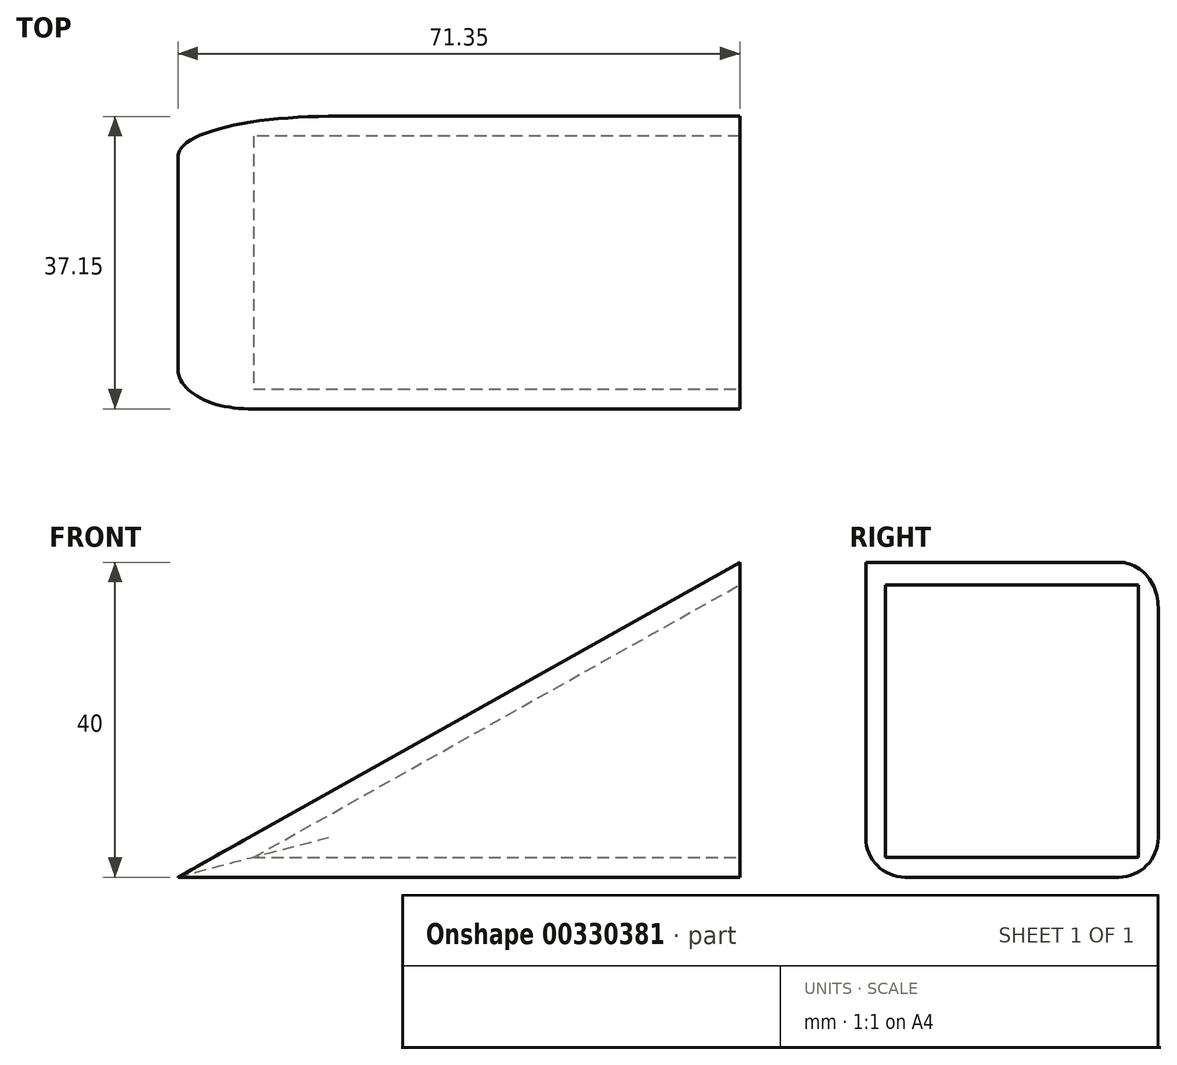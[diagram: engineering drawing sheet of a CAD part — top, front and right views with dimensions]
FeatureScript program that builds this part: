
annotation { "Feature Type Name" : "Feature", "Feature Type Description" : "" }
export const myFeature = defineFeature(function(context is Context, id is Id, definition is map)
    precondition{}
    {
        {
            var Q0;
            Q0=qCreatedBy(makeId("Top.planeOp"),FACE);
            var sketch = newSketch(context, id + "F0", { "sketchPlane" : qUnion([Q0])});
            skLineSegment(sketch, "E0.bottom", {"start": v(-52.14, 32.68) * mm, "end": v(19.21, 32.68) * mm});
            skLineSegment(sketch, "E0.top", {"start": v(-52.14, -4.47) * mm, "end": v(19.21, -4.47) * mm});
            skLineSegment(sketch, "E0.left", {"start": v(-52.14, 32.68) * mm, "end": v(-52.14, -4.47) * mm});
            skLineSegment(sketch, "E0.right", {"start": v(19.21, 32.68) * mm, "end": v(19.21, -4.47) * mm});
            skSolve(sketch);
        }
        {
            var Q0;
            Q0=makeQuery(id+"F0.imprint","IMPRINT",FACE,{"disambiguationData":[TD([[makeQuery(id+"F0.imprint","IMPRINT",EDGE,{"derivedFrom":sQuery(id+"F0.wireOp",EDGE,"E0.bottom")}),-1.0]])]});
            extrude(context, id + "F1", {"entities" : qUnion([Q0]), "depth" : 40 * mm});
        }
        {
            var Q0;
            Q0=makeQuery(id+"F1.opExtrude","SWEPT_FACE",FACE,{"disambiguationData":[OSD([sQuery(id+"F0.wireOp",EDGE,"E0.top")])]});
            var sketch = newSketch(context, id + "F2", { "sketchPlane" : qUnion([Q0])});
            skLineSegment(sketch, "E1", {"start": v(-52.14, 0) * mm, "end": v(19.21, 40) * mm});
            skSolve(sketch);
        }
        {
            var Q0;
            Q0=makeQuery(id+"F2.imprint","IMPRINT",FACE,{"disambiguationData":[TD([[makeQuery(id+"F2.imprint","IMPRINT",EDGE,{"derivedFrom":sQuery(id+"F2.wireOp",EDGE,"E1")}),1.0]])]});
            extrude(context, id + "F3", {"entities" : qUnion([Q0]), "operationType" : NewBodyOperationType.REMOVE, "oppositeDirection" : true, "depth" : 25 * mm});
        }
        {
            var Q0;
            Q0=makeQuery(id+"F3.boolean.opBoolean","COPY",FACE,{"derivedFrom":makeQuery(id+"F3.opExtrude","CAP_FACE",FACE,{"disambiguationData":[OSD([sQuery(id+"F0.wireOp",EDGE,"E0.top"),sQuery(id+"F0.wireOp",EDGE,"E0.left"),sQuery(id+"F2.wireOp",EDGE,"E1")])],"isStart":false})});
            extrude(context, id + "F4", {"entities" : qUnion([Q0]), "operationType" : NewBodyOperationType.REMOVE, "endBound" : BoundingType.THROUGH_ALL, "oppositeDirection" : true, "depth" : 25 * mm});
        }
        {
            var Q0;
            Q0=makeQuery(id+"F1.opExtrude","SWEPT_FACE",FACE,{"disambiguationData":[OSD([sQuery(id+"F0.wireOp",EDGE,"E0.right")])]});
            shell(context, id + "F5", {"entities" : qUnion([Q0]), "thickness" : 2.5 * mm});
        }
        {
            var Q0;
            Q0=makeQuery(id+"F4.boolean.opBoolean","INTERSECT",EDGE,{"derivedFrom":[makeQuery(id+"F1.opExtrude","SWEPT_FACE",FACE,{"disambiguationData":[OSD([sQuery(id+"F0.wireOp",EDGE,"E0.bottom")])]}),makeQuery(id+"F4.opExtrude","SWEPT_FACE",FACE,{"disambiguationData":[OSD([sQuery(id+"F2.wireOp",EDGE,"E1")])]})]});
            var Q1;
            Q1=makeQuery(id+"F1.opExtrude","CAP_EDGE",EDGE,{"disambiguationData":[OSD([sQuery(id+"F0.wireOp",EDGE,"E0.bottom")])],"isStart":true});
            var Q2;
            Q2=makeQuery(id+"F3.boolean.opBoolean","COPY",EDGE,{"derivedFrom":makeQuery(id+"F3.opExtrude","CAP_EDGE",EDGE,{"disambiguationData":[OSD([sQuery(id+"F2.wireOp",EDGE,"E1")])],"isStart":true})});
            var Q3;
            Q3=makeQuery(id+"F1.opExtrude","CAP_EDGE",EDGE,{"disambiguationData":[OSD([sQuery(id+"F0.wireOp",EDGE,"E0.top")])],"isStart":true});
            fillet(context, id + "F6", {"entities" : qUnion([Q0, Q1, Q2, Q3]), "radius" : 5 * mm, "tangentPropagation" : true, "allowEdgeOverflow" : false});
        }
    });
